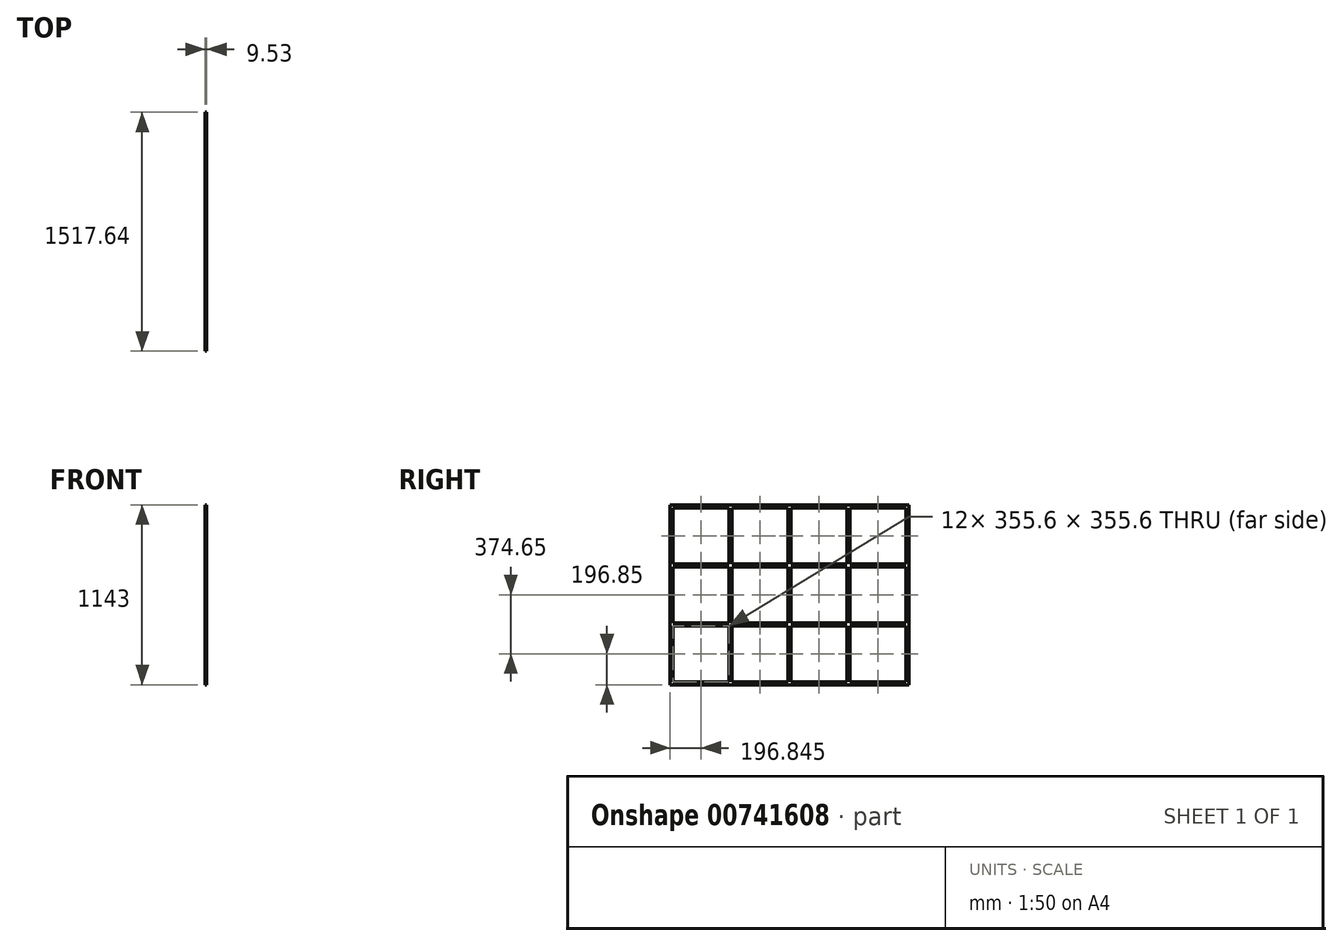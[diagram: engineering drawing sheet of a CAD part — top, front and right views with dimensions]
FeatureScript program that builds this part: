
annotation { "Feature Type Name" : "Feature", "Feature Type Description" : "" }
export const myFeature = defineFeature(function(context is Context, id is Id, definition is map)
    precondition{}
    {
        {
            var Q0;
            Q0=qCreatedBy(makeId("Right.planeOp"),FACE);
            var sketch = newSketch(context, id + "F0", { "sketchPlane" : qUnion([Q0])});
            skLineSegment(sketch, "E0.bottom", {"start": v(758.83, 571.5) * mm, "end": v(-758.83, 571.5) * mm});
            skLineSegment(sketch, "E0.top", {"start": v(758.83, -571.5) * mm, "end": v(-758.82, -571.5) * mm});
            skLineSegment(sketch, "E0.left", {"start": v(758.83, 571.5) * mm, "end": v(758.83, -571.5) * mm});
            skLineSegment(sketch, "E0.right", {"start": v(-758.83, 571.5) * mm, "end": v(-758.82, -571.5) * mm});
            skPoint(sketch, "E0.middle", {"position": v(0, 0) * mm});
            skLineSegment(sketch, "E1.bottom", {"start": v(-758.83, 571.5) * mm, "end": v(-739.78, 571.5) * mm});
            skLineSegment(sketch, "E1.left", {"start": v(-758.83, 571.5) * mm, "end": v(-758.83, 552.45) * mm});
            skLineSegment(sketch, "E2.bottom", {"start": v(-739.78, 552.45) * mm, "end": v(-384.18, 552.45) * mm});
            skLineSegment(sketch, "E2.top", {"start": v(-739.78, -552.45) * mm, "end": v(-384.18, -552.45) * mm});
            skLineSegment(sketch, "E2.left", {"start": v(-739.78, 552.45) * mm, "end": v(-739.78, 196.85) * mm});
            skLineSegment(sketch, "E2.right", {"start": v(739.77, 552.45) * mm, "end": v(739.77, 196.85) * mm});
            skLineSegment(sketch, "E3", {"start": v(739.77, 552.45) * mm, "end": v(384.17, 552.45) * mm});
            skLineSegment(sketch, "E4.right", {"start": v(-365.12, -552.45) * mm, "end": v(-365.13, -196.85) * mm});
            skLineSegment(sketch, "E5.left", {"start": v(384.17, 552.45) * mm, "end": v(384.17, 196.85) * mm});
            skLineSegment(sketch, "E5.right", {"start": v(365.12, 552.45) * mm, "end": v(365.12, 196.85) * mm});
            skLineSegment(sketch, "E6.bottom", {"start": v(-384.18, 552.45) * mm, "end": v(-739.78, 552.45) * mm});
            skLineSegment(sketch, "E6.top", {"start": v(-384.18, 196.85) * mm, "end": v(-739.78, 196.85) * mm});
            skLineSegment(sketch, "E6.left", {"start": v(-384.18, 552.45) * mm, "end": v(-384.18, 196.85) * mm});
            skLineSegment(sketch, "E7.top", {"start": v(-739.78, -196.85) * mm, "end": v(-384.18, -196.85) * mm});
            skLineSegment(sketch, "E7.left", {"start": v(-739.78, -552.45) * mm, "end": v(-739.78, -196.85) * mm});
            skLineSegment(sketch, "E7.right", {"start": v(-384.18, -552.45) * mm, "end": v(-384.18, -196.85) * mm});
            skLineSegment(sketch, "E8.bottom", {"start": v(-365.13, 552.45) * mm, "end": v(-9.53, 552.45) * mm});
            skLineSegment(sketch, "E8.top", {"start": v(-365.13, 196.85) * mm, "end": v(-9.53, 196.85) * mm});
            skLineSegment(sketch, "E8.left", {"start": v(-365.13, 552.45) * mm, "end": v(-365.13, 196.85) * mm});
            skLineSegment(sketch, "E8.right", {"start": v(-9.53, 552.45) * mm, "end": v(-9.53, 196.85) * mm});
            skLineSegment(sketch, "E9.bottom", {"start": v(-365.12, -552.45) * mm, "end": v(-9.52, -552.45) * mm});
            skLineSegment(sketch, "E9.top", {"start": v(-365.13, -196.85) * mm, "end": v(-9.53, -196.85) * mm});
            skLineSegment(sketch, "E9.left", {"start": v(-365.12, -552.45) * mm, "end": v(-365.12, -196.85) * mm});
            skLineSegment(sketch, "E9.right", {"start": v(-9.52, -552.45) * mm, "end": v(-9.53, -196.85) * mm});
            skLineSegment(sketch, "E10.bottom", {"start": v(384.17, 552.45) * mm, "end": v(739.77, 552.45) * mm});
            skLineSegment(sketch, "E10.top", {"start": v(384.18, 196.85) * mm, "end": v(739.78, 196.85) * mm});
            skLineSegment(sketch, "E11.bottom", {"start": v(384.17, -552.45) * mm, "end": v(739.77, -552.45) * mm});
            skLineSegment(sketch, "E11.top", {"start": v(384.18, -196.85) * mm, "end": v(739.78, -196.85) * mm});
            skLineSegment(sketch, "E11.left", {"start": v(384.17, -552.45) * mm, "end": v(384.17, -196.85) * mm});
            skLineSegment(sketch, "E11.right", {"start": v(739.77, -552.45) * mm, "end": v(739.77, -196.85) * mm});
            skLineSegment(sketch, "E12.bottom", {"start": v(365.13, -552.45) * mm, "end": v(9.53, -552.45) * mm});
            skLineSegment(sketch, "E12.top", {"start": v(365.13, -196.85) * mm, "end": v(9.53, -196.85) * mm});
            skLineSegment(sketch, "E12.left", {"start": v(365.13, -552.45) * mm, "end": v(365.13, -196.85) * mm});
            skLineSegment(sketch, "E12.right", {"start": v(9.53, -552.45) * mm, "end": v(9.53, -196.85) * mm});
            skLineSegment(sketch, "E13", {"start": v(-9.53, -177.8) * mm, "end": v(-9.53, 177.8) * mm});
            skLineSegment(sketch, "E14", {"start": v(9.53, -177.8) * mm, "end": v(9.53, 177.8) * mm});
            skLineSegment(sketch, "E15", {"start": v(365.12, 196.85) * mm, "end": v(9.53, 196.85) * mm});
            skLineSegment(sketch, "E16.bottom", {"start": v(-739.78, -177.8) * mm, "end": v(-384.18, -177.8) * mm});
            skLineSegment(sketch, "E16.top", {"start": v(-739.78, 177.8) * mm, "end": v(-384.18, 177.8) * mm});
            skLineSegment(sketch, "E16.left", {"start": v(-739.78, -177.8) * mm, "end": v(-739.78, 177.8) * mm});
            skLineSegment(sketch, "E16.right", {"start": v(739.77, -177.8) * mm, "end": v(739.77, 177.8) * mm});
            skLineSegment(sketch, "E17.trimOffspring", {"start": v(-739.78, 177.8) * mm, "end": v(-739.78, -177.8) * mm});
            skLineSegment(sketch, "E18.trimOffspring", {"start": v(-384.18, 196.85) * mm, "end": v(-384.18, 552.45) * mm});
            skLineSegment(sketch, "E19.trimOffspring", {"start": v(-365.13, 196.85) * mm, "end": v(-365.13, 552.45) * mm});
            skLineSegment(sketch, "E20.trimOffspring", {"start": v(-365.13, 177.8) * mm, "end": v(-9.53, 177.8) * mm});
            skLineSegment(sketch, "E21.trimOffspring", {"start": v(9.53, 177.8) * mm, "end": v(365.12, 177.8) * mm});
            skLineSegment(sketch, "E22.trimOffspring", {"start": v(9.53, 196.85) * mm, "end": v(9.53, 552.45) * mm});
            skLineSegment(sketch, "E23.trimOffspring", {"start": v(365.12, 177.8) * mm, "end": v(365.13, -177.8) * mm});
            skLineSegment(sketch, "E24.trimOffspring", {"start": v(384.17, 177.8) * mm, "end": v(739.78, 177.8) * mm});
            skLineSegment(sketch, "E25.trimOffspring", {"start": v(384.17, 177.8) * mm, "end": v(384.17, -177.8) * mm});
            skLineSegment(sketch, "E26.trimOffspring", {"start": v(739.77, 177.8) * mm, "end": v(739.77, -177.8) * mm});
            skLineSegment(sketch, "E27.trimOffspring", {"start": v(384.18, 552.45) * mm, "end": v(739.77, 552.45) * mm});
            skLineSegment(sketch, "E28.trimOffspring", {"start": v(9.53, 552.45) * mm, "end": v(365.12, 552.45) * mm});
            skLineSegment(sketch, "E29.trimOffspring", {"start": v(-739.78, -196.85) * mm, "end": v(-739.78, -552.45) * mm});
            skLineSegment(sketch, "E30.trimOffspring", {"start": v(-384.18, -177.8) * mm, "end": v(-384.18, 177.8) * mm});
            skLineSegment(sketch, "E31.trimOffspring", {"start": v(-365.13, -177.8) * mm, "end": v(-9.53, -177.8) * mm});
            skLineSegment(sketch, "E32.trimOffspring", {"start": v(-365.13, -177.8) * mm, "end": v(-365.13, 177.8) * mm});
            skLineSegment(sketch, "E33.trimOffspring", {"start": v(9.53, -177.8) * mm, "end": v(365.13, -177.8) * mm});
            skLineSegment(sketch, "E34.trimOffspring", {"start": v(365.13, -196.85) * mm, "end": v(365.13, -552.45) * mm});
            skLineSegment(sketch, "E35.trimOffspring", {"start": v(384.17, -177.8) * mm, "end": v(739.78, -177.8) * mm});
            skLineSegment(sketch, "E36.trimOffspring", {"start": v(384.17, -196.85) * mm, "end": v(384.17, -552.45) * mm});
            skLineSegment(sketch, "E37.trimOffspring", {"start": v(739.77, -196.85) * mm, "end": v(739.77, -552.45) * mm});
            skLineSegment(sketch, "E38.trimOffspring", {"start": v(384.18, -552.45) * mm, "end": v(739.78, -552.45) * mm});
            skLineSegment(sketch, "E39.trimOffspring", {"start": v(9.53, -552.45) * mm, "end": v(365.13, -552.45) * mm});
            skSolve(sketch);
        }
        {
            var Q0;
            Q0 = qSketchRegion(id + "F0", true);
            extrude(context, id + "F1", {"entities" : qUnion([Q0]), "depth" : 9.52 * mm, "offsetDistance" : 25.4 * mm});
        }
    });
